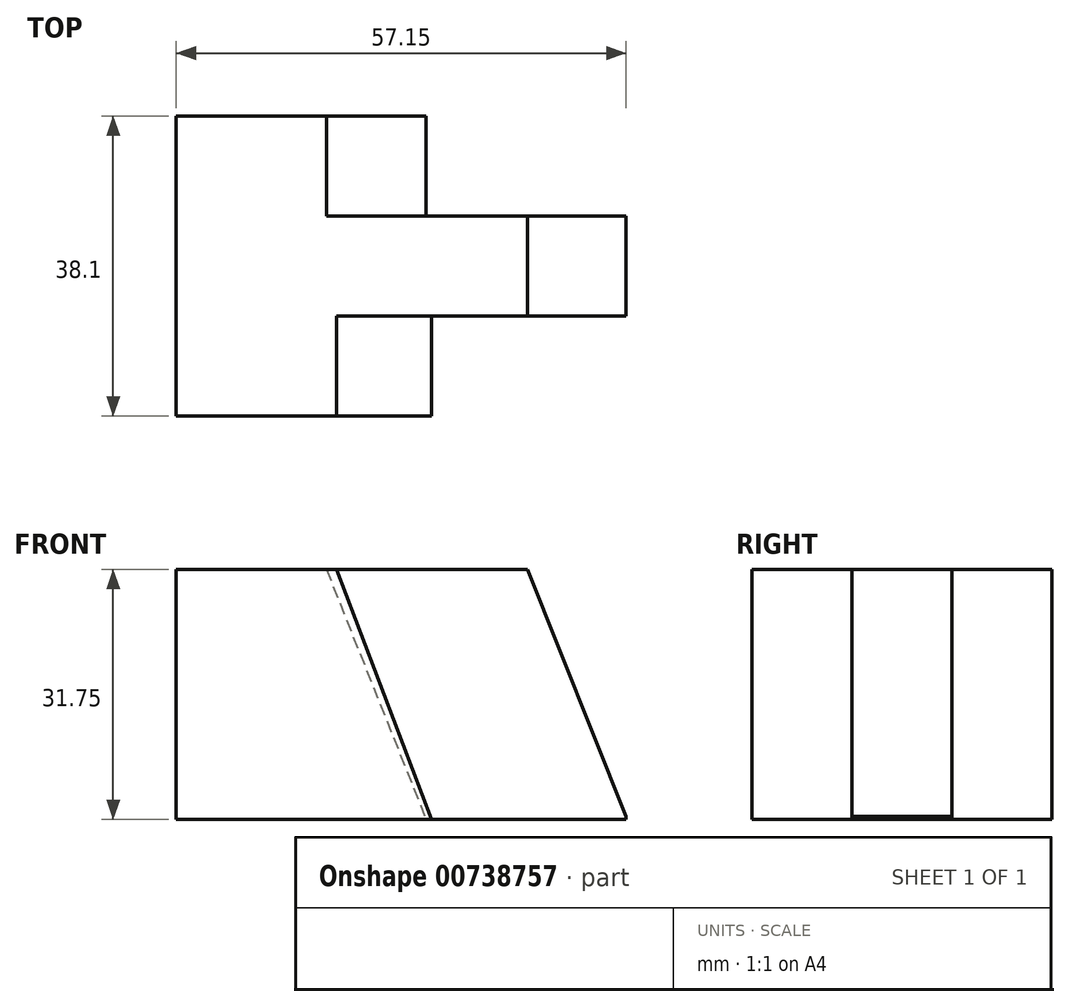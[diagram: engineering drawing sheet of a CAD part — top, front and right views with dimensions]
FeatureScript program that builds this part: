
annotation { "Feature Type Name" : "Feature", "Feature Type Description" : "" }
export const myFeature = defineFeature(function(context is Context, id is Id, definition is map)
    precondition{}
    {
        {
            var Q0;
            Q0=qCreatedBy(makeId("Front.planeOp"),FACE);
            var sketch = newSketch(context, id + "F0", { "sketchPlane" : qUnion([Q0])});
            skLineSegment(sketch, "E0", {"start": v(0, 0) * mm, "end": v(0, 31.75) * mm});
            skLineSegment(sketch, "E1", {"start": v(0, 31.75) * mm, "end": v(57.15, 31.75) * mm});
            skLineSegment(sketch, "E2", {"start": v(57.15, 31.75) * mm, "end": v(57.15, 0) * mm});
            skLineSegment(sketch, "E3", {"start": v(57.15, 0) * mm, "end": v(0, 0) * mm});
            skSolve(sketch);
        }
        {
            var Q0;
            Q0 = qSketchRegion(id + "F0", true);
            extrude(context, id + "F1", {"entities" : qUnion([Q0]), "depth" : 38.1 * mm, "offsetDistance" : 25.4 * mm});
        }
        {
            var Q0;
            Q0=qCreatedBy(makeId("Front.planeOp"),FACE);
            var sketch = newSketch(context, id + "F2", { "sketchPlane" : qUnion([Q0])});
            skLineSegment(sketch, "E4", {"start": v(19.05, 31.83) * mm, "end": v(31.75, 0) * mm});
            skLineSegment(sketch, "E5", {"start": v(31.75, 0) * mm, "end": v(57.15, 0) * mm});
            skLineSegment(sketch, "E6", {"start": v(57.15, 0) * mm, "end": v(57.15, 31.75) * mm});
            skLineSegment(sketch, "E7", {"start": v(57.15, 31.75) * mm, "end": v(19.05, 31.83) * mm});
            skSolve(sketch);
        }
        {
            var Q0;
            Q0 = qSketchRegion(id + "F2", true);
            extrude(context, id + "F3", {"entities" : qUnion([Q0]), "operationType" : NewBodyOperationType.REMOVE, "depth" : 12.7 * mm, "offsetDistance" : 25.4 * mm});
        }
        {
            var Q0;
            Q0=makeQuery(id+"F1.opExtrude","CAP_FACE",FACE,{"disambiguationData":[OSD([sQuery(id+"F0.wireOp",EDGE,"E0"),sQuery(id+"F0.wireOp",EDGE,"E1"),sQuery(id+"F0.wireOp",EDGE,"E2"),sQuery(id+"F0.wireOp",EDGE,"E3")])],"isStart":false});
            var sketch = newSketch(context, id + "F4", { "sketchPlane" : qUnion([Q0])});
            skLineSegment(sketch, "E8", {"start": v(20.34, 31.75) * mm, "end": v(32.44, 0) * mm});
            skSolve(sketch);
        }
        {
            var Q0;
            {var subQ0=sQuery(id+"F4.wireOp",EDGE,"E8");Q0=makeQuery(id+"F4.imprint","IMPRINT",FACE,{"disambiguationData":[TD([[makeQuery(id+"F4.imprint","IMPRINT",EDGE,{"derivedFrom":subQ0}),1.0]])]});}
            extrude(context, id + "F5", {"entities" : qUnion([Q0]), "operationType" : NewBodyOperationType.REMOVE, "oppositeDirection" : true, "depth" : 12.7 * mm, "offsetDistance" : 25.4 * mm});
        }
        {
            var Q0;
            Q0=qCreatedBy(makeId("Front.planeOp"),FACE);
            var sketch = newSketch(context, id + "F6", { "sketchPlane" : qUnion([Q0])});
            skLineSegment(sketch, "E9", {"start": v(57.3, 0) * mm, "end": v(57.3, 31.75) * mm});
            skLineSegment(sketch, "E10", {"start": v(57.3, 31.75) * mm, "end": v(44.6, 31.75) * mm});
            skLineSegment(sketch, "E11", {"start": v(44.6, 31.75) * mm, "end": v(57.3, 0) * mm});
            skSolve(sketch);
        }
        {
            var Q0;
            Q0 = qSketchRegion(id + "F6", true);
            extrude(context, id + "F7", {"entities" : qUnion([Q0]), "operationType" : NewBodyOperationType.REMOVE, "endBound" : BoundingType.THROUGH_ALL, "depth" : 25.4 * mm, "offsetDistance" : 25.4 * mm});
        }
    });
